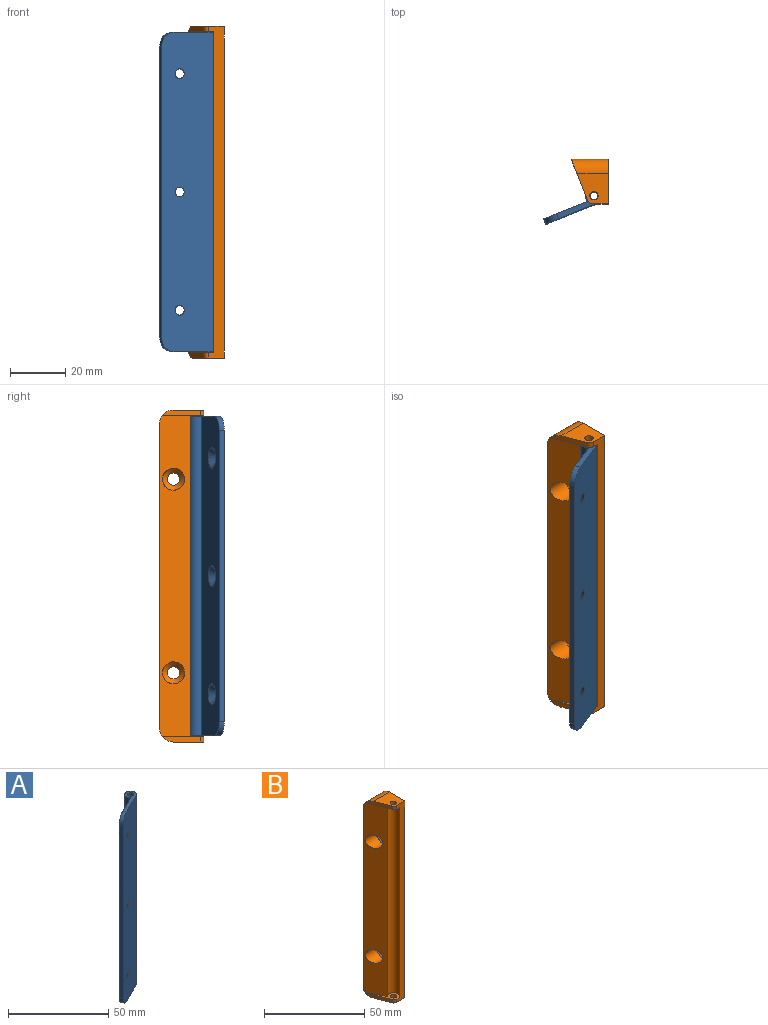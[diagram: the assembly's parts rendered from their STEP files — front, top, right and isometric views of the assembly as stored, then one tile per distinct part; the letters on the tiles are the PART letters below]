
ASSEMBLY  parts=2 mates=1
PART A: 12 faces, bbox 20.5x14.5x115.5 mm
  f0: plane 115.5x17.98mm, normal (0.44,-0.9,0), area 2270.4mm2, adj f1,f4,f5,f6,f7,f8,f9,f10
  f1: cylinder r=3mm len=115.5mm, axis (0,0,-1), area 1750.6mm2, adj f0,f2,f5,f6
  f2: plane 115.5x15.43mm, normal (-0.44,0.9,0), area 1840.1mm2, adj f1,f4,f5,f6,f7,f8,f9,f10
  f3: cylinder r=1.5mm len=115.5mm, axis (0,0,-1), area 1088.6mm2, adj f5,f6
  f4: plane 105.5x1.8mm, normal (-0.9,-0.44,0), area 211mm2, adj f0,f2,f10,f11
  f5: plane 16.04x12.27mm, normal (0,0,1), area 47.1mm2, adj f0,f1,f2,f3,f11
  f6: plane 16.04x12.27mm, normal (0,0,-1), area 47.1mm2, adj f0,f1,f2,f3,f10
  f7: cone r=1.75mm half-angle=45deg, axis (-0.44,0.9,0), area 48.9mm2, adj f0,f2
  f8: cone r=1.75mm half-angle=45deg, axis (-0.44,0.9,0), area 48.9mm2, adj f0,f2
  f9: cone r=1.75mm half-angle=45deg, axis (-0.44,0.9,0), area 48.9mm2, adj f0,f2
  f10: cylinder r=5mm len=5.37mm, axis (0.44,-0.9,0), area 15.7mm2, adj f0,f2,f4,f6
  f11: cylinder r=5mm len=5.37mm, axis (-0.44,0.9,0), area 15.7mm2, adj f0,f2,f4,f5
PART B: 23 faces, bbox 13.4x16x120 mm
  f0: plane 13.82x5.51mm, normal (-0.93,-0.37,0), area 27.2mm2, adj f2,f10,f14,f21
  f1: plane 120x5.73mm, normal (0,-1,0), area 473.6mm2, adj f2,f4,f7,f9,f10,f11,f13,f14
  f2: cylinder r=1.87mm len=2mm, axis (0,0,-1), area 4.5mm2, adj f0,f1,f10,f14
  f3: cylinder r=1.5mm len=3mm, axis (0,0,-1), area 18.8mm2, adj f10,f14
  f4: plane 120x16mm, normal (1,0,0), area 1877.5mm2, adj f1,f5,f9,f10,f15,f16,f21,f22
  f5: plane 110x13.38mm, normal (0,1,0), area 1472.1mm2, adj f4,f12,f21,f22
  f6: plane 13.82x5.51mm, normal (-0.93,-0.37,0), area 27.2mm2, adj f7,f9,f13,f22
  f7: cylinder r=1.87mm len=2mm, axis (0,0,-1), area 4.5mm2, adj f1,f6,f9,f13
  f8: cylinder r=1.5mm len=3mm, axis (0,0,-1), area 18.8mm2, adj f9,f13
  f9: plane 11.39x11mm, normal (0,0,1), area 93.8mm2, adj f1,f4,f6,f7,f8,f22
  f10: plane 11.39x11mm, normal (0,0,-1), area 93.8mm2, adj f0,f1,f2,f3,f4,f21
  f11: cylinder r=3.15mm len=116mm, axis (0,0,-1), area 1287.5mm2, adj f1,f12,f13,f14
  f12: plane 116x10.97mm, normal (-0.88,-0.47,0), area 1328.5mm2, adj f5,f11,f13,f14,f17,f18,f21,f22
  f13: plane 15x10.93mm, normal (0,0,-1), area 31.9mm2, adj f1,f6,f7,f8,f11,f12,f22
  f14: plane 15x10.93mm, normal (0,0,1), area 31.9mm2, adj f0,f1,f2,f3,f11,f12,f21
  f15: cylinder r=2.25mm len=4.5mm, axis (1,0,0), area 42.4mm2, adj f4,f20
  f16: cylinder r=2.25mm len=4.5mm, axis (1,0,0), area 42.4mm2, adj f4,f19
  f17: cylinder r=4mm len=8.13mm, axis (1,0,0), area 149.4mm2, adj f12,f19
  f18: cylinder r=4mm len=8.13mm, axis (1,0,0), area 149.4mm2, adj f12,f20
  f19: cone r=4.25mm half-angle=45deg, axis (-1,0,0), area 48.6mm2, adj f16,f17
  f20: cone r=4.25mm half-angle=45deg, axis (-1,0,0), area 48.6mm2, adj f15,f18
  f21: cylinder r=5mm len=13.38mm, axis (-1,0,0), area 99.3mm2, adj f0,f4,f5,f10,f12,f14
  f22: cylinder r=5mm len=13.38mm, axis (1,0,0), area 99.3mm2, adj f4,f5,f6,f9,f12,f13
PLACE A rot(axis=(0,0,-1),4.1deg) t=(0,0,0)mm
PLACE B at identity fixed
MATE revolute B.f3 <-> A.f1  axis (0,0,-1) through (0,0,58)mm
